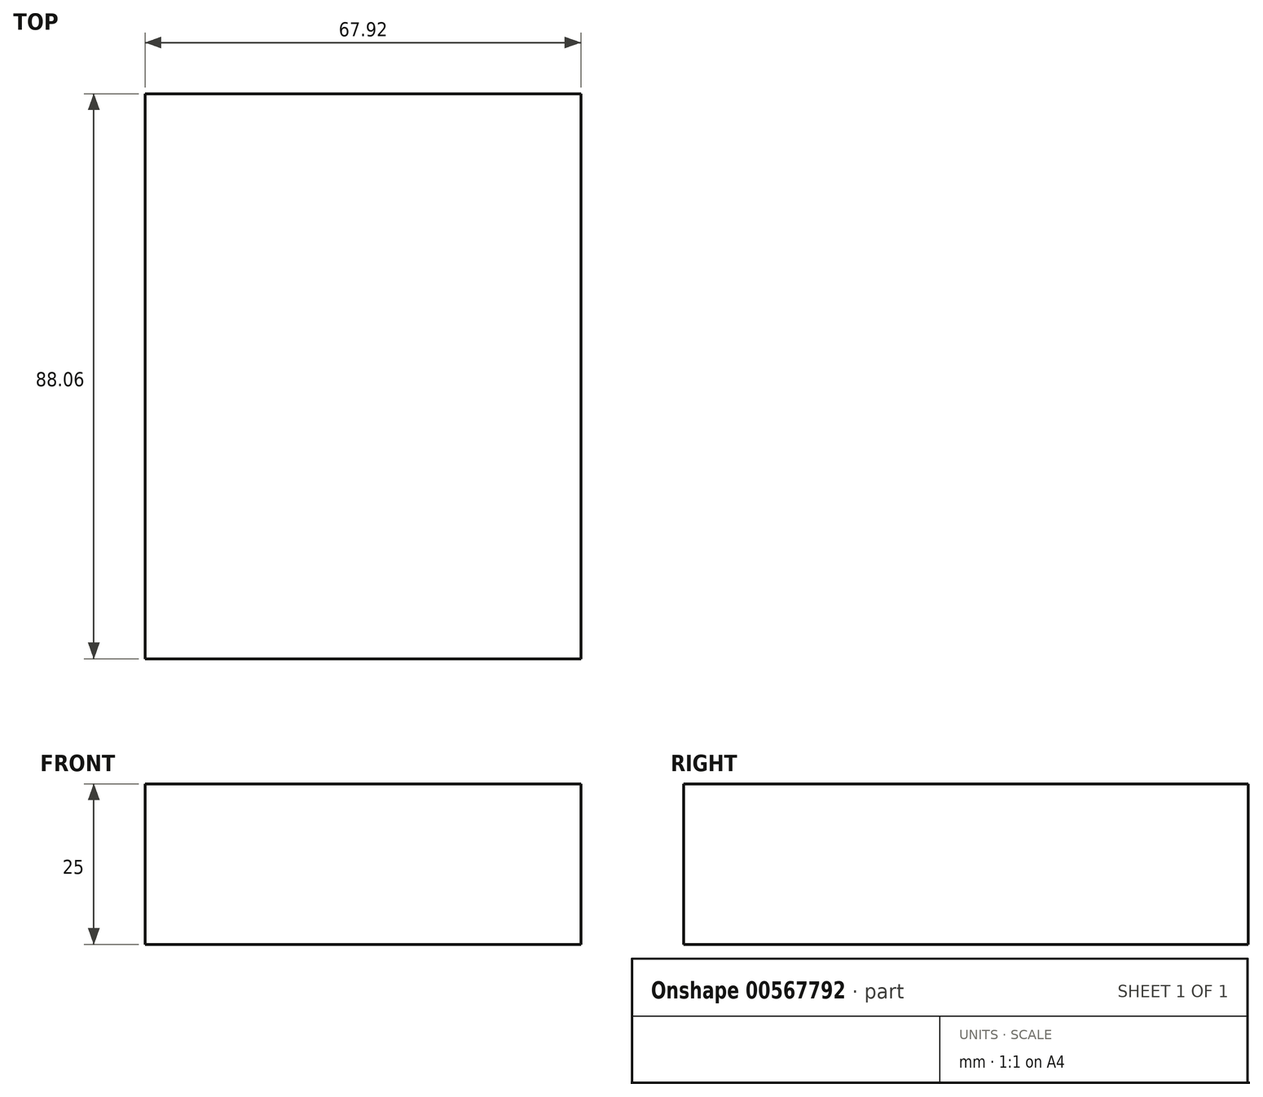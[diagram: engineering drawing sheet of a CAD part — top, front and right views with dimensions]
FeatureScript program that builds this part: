
annotation { "Feature Type Name" : "Feature", "Feature Type Description" : "" }
export const myFeature = defineFeature(function(context is Context, id is Id, definition is map)
    precondition{}
    {
        {
            var Q0;
            Q0=qCreatedBy(makeId("Top.planeOp"),FACE);
            var sketch = newSketch(context, id + "F0", { "sketchPlane" : qUnion([Q0])});
            skLineSegment(sketch, "E0.bottom", {"start": v(33.96, 44.03) * mm, "end": v(-33.96, 44.03) * mm});
            skLineSegment(sketch, "E0.top", {"start": v(33.96, -44.03) * mm, "end": v(-33.96, -44.03) * mm});
            skLineSegment(sketch, "E0.left", {"start": v(33.96, 44.03) * mm, "end": v(33.96, -44.03) * mm});
            skLineSegment(sketch, "E0.right", {"start": v(-33.96, 44.03) * mm, "end": v(-33.96, -44.03) * mm});
            skPoint(sketch, "E0.middle", {"position": v(0, 0) * mm});
            skSolve(sketch);
        }
        {
            var Q0;
            Q0=makeQuery(id+"F0.imprint","IMPRINT",FACE,{"disambiguationData":[TD([[makeQuery(id+"F0.imprint","IMPRINT",EDGE,{"derivedFrom":sQuery(id+"F0.wireOp",EDGE,"E0.bottom")}),1.0]])]});
            extrude(context, id + "F1", {"entities" : qUnion([Q0]), "depth" : 25 * mm, "offsetDistance" : 25 * mm});
        }
    });
